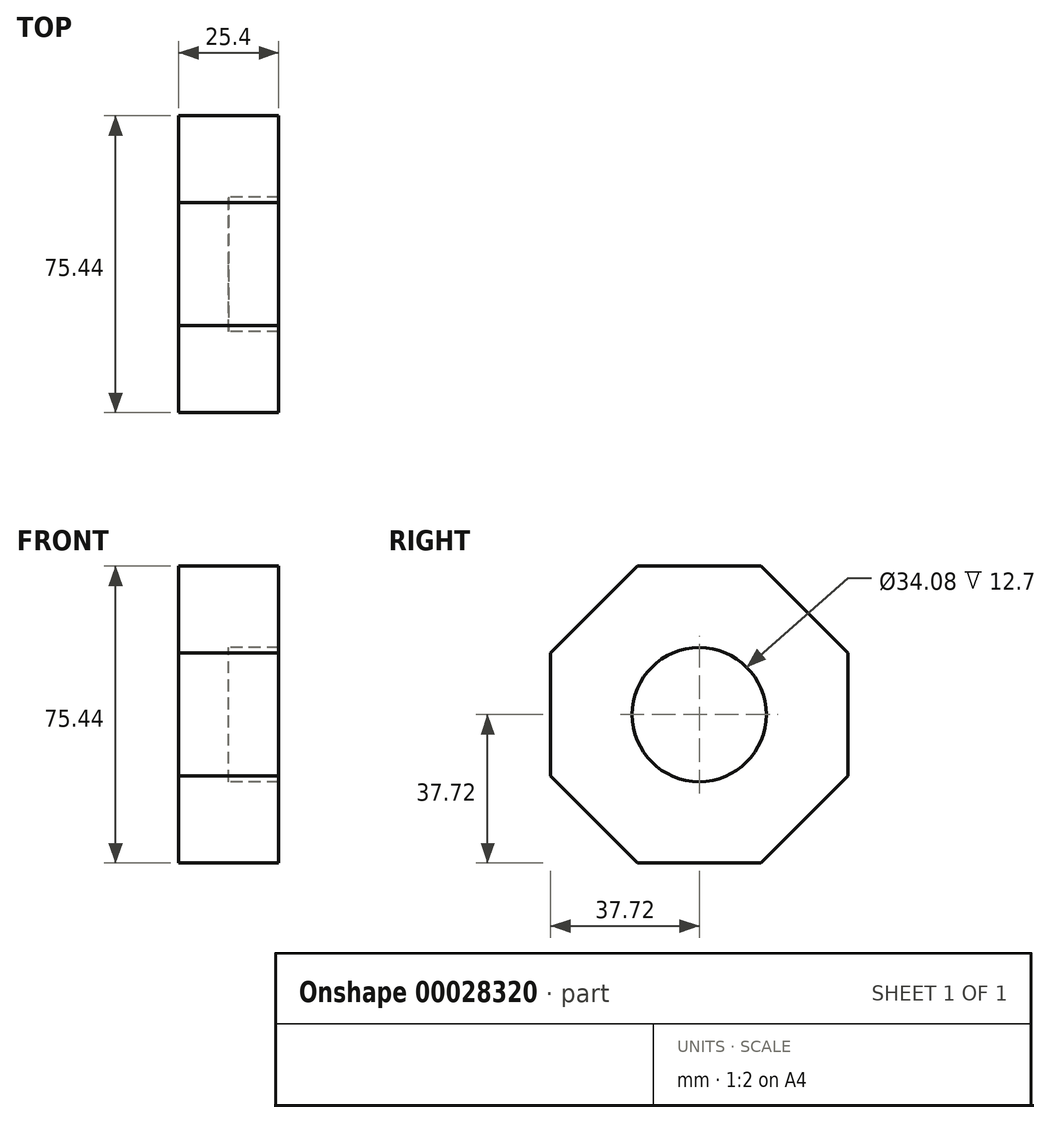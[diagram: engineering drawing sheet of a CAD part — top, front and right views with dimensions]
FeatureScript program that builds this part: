
annotation { "Feature Type Name" : "Feature", "Feature Type Description" : "" }
export const myFeature = defineFeature(function(context is Context, id is Id, definition is map)
    precondition{}
    {
        {
            var Q0;
            Q0=qCreatedBy(makeId("Right.planeOp"),FACE);
            var sketch = newSketch(context, id + "F0", { "sketchPlane" : qUnion([Q0])});
            skCircle(sketch, "E0.cCircle", {"center": v(0, 0) * mm, "radius": 37.72 * mm, "construction": true});
            skLineSegment(sketch, "E0.0", {"start": v(37.72, 15.62) * mm, "end": v(37.72, -15.62) * mm});
            skLineSegment(sketch, "E0.1", {"start": v(37.72, -15.62) * mm, "end": v(15.62, -37.72) * mm});
            skLineSegment(sketch, "E0.2", {"start": v(15.62, -37.72) * mm, "end": v(-15.62, -37.72) * mm});
            skLineSegment(sketch, "E0.3", {"start": v(-15.62, -37.72) * mm, "end": v(-37.72, -15.62) * mm});
            skLineSegment(sketch, "E0.4", {"start": v(-37.72, -15.62) * mm, "end": v(-37.72, 15.62) * mm});
            skLineSegment(sketch, "E0.5", {"start": v(-37.72, 15.62) * mm, "end": v(-15.62, 37.72) * mm});
            skLineSegment(sketch, "E0.6", {"start": v(-15.62, 37.72) * mm, "end": v(15.62, 37.72) * mm});
            skLineSegment(sketch, "E0.7", {"start": v(15.62, 37.72) * mm, "end": v(37.72, 15.62) * mm});
            skCircle(sketch, "E1", {"center": v(0, 0) * mm, "radius": 17.04 * mm});
            skSolve(sketch);
        }
        {
            var Q0;
            Q0 = qSketchRegion(id + "F0", true);
            extrude(context, id + "F1", {"entities" : qUnion([Q0]), "depth" : 12.7 * mm});
        }
        {
            var Q0;
            Q0 = qSketchRegion(id + "F0", true);
            extrude(context, id + "F2", {"entities" : qUnion([Q0]), "operationType" : NewBodyOperationType.ADD, "depth" : 25.4 * mm});
        }
        {
            var Q0;
            Q0=makeQuery(id+"F0.imprint","IMPRINT",FACE,{"disambiguationData":[TD([[makeQuery(id+"F0.imprint","IMPRINT",EDGE,{"derivedFrom":sQuery(id+"F0.wireOp",EDGE,"E1")}),1.0]])]});
            extrude(context, id + "F3", {"entities" : qUnion([Q0]), "operationType" : NewBodyOperationType.ADD, "depth" : 12.7 * mm});
        }
    });
